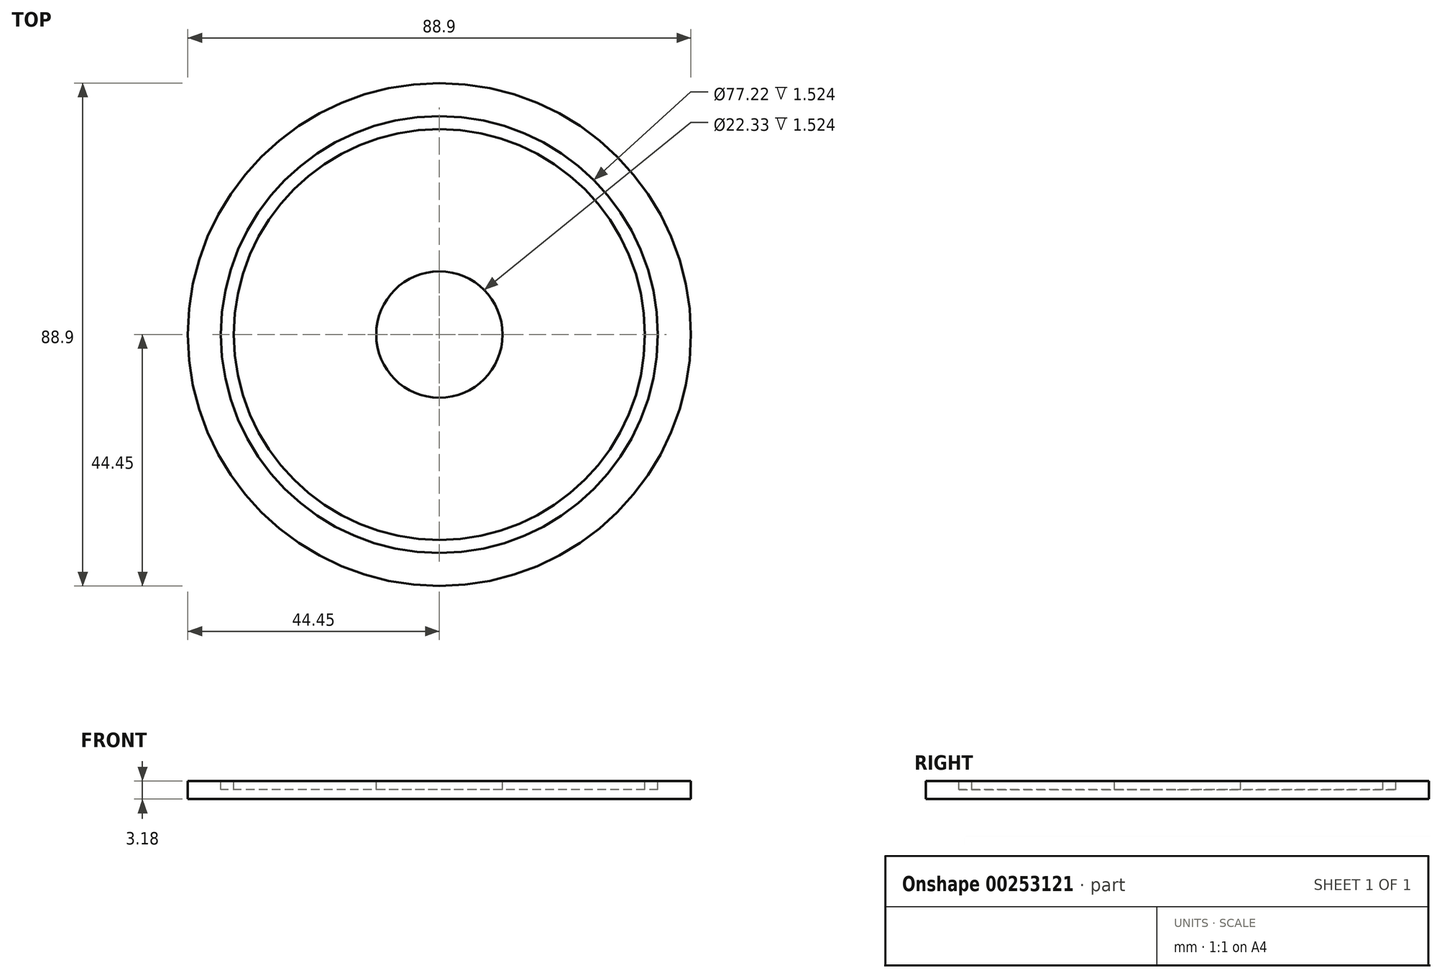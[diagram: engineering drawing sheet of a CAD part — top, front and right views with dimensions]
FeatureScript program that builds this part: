
annotation { "Feature Type Name" : "Feature", "Feature Type Description" : "" }
export const myFeature = defineFeature(function(context is Context, id is Id, definition is map)
    precondition{}
    {
        {
            var Q0;
            Q0=qCreatedBy(makeId("Top.planeOp"),FACE);
            var sketch = newSketch(context, id + "F0", { "sketchPlane" : qUnion([Q0])});
            skCircle(sketch, "E0", {"center": v(0, 0) * mm, "radius": 44.45 * mm});
            skSolve(sketch);
        }
        {
            var Q0;
            Q0=qSketchRegion(id+"F0",true);
            extrude(context, id + "F1", {"entities" : qUnion([Q0]), "depth" : 3.17 * mm});
        }
        {
            var Q0;
            Q0=makeQuery(id+"F1.opExtrude","CAP_FACE",FACE,{"disambiguationData":[OSD([sQuery(id+"F0.wireOp",EDGE,"E0")])],"isStart":false});
            var sketch = newSketch(context, id + "F2", { "sketchPlane" : qUnion([Q0])});
            skCircle(sketch, "E1", {"center": v(0, 0) * mm, "radius": 38.6 * mm});
            skCircle(sketch, "E2", {"center": v(0, 0) * mm, "radius": 36.32 * mm});
            skCircle(sketch, "E3", {"center": v(0, 0) * mm, "radius": 11.16 * mm});
            skSolve(sketch);
        }
        {
            var Q0;
            Q0=qSketchRegion(id+"F2",true);
            var Q1;
            Q1=makeQuery(id+"F2.imprint","IMPRINT",FACE,{"disambiguationData":[TD([[makeQuery(id+"F2.imprint","IMPRINT",EDGE,{"derivedFrom":sQuery(id+"F2.wireOp",EDGE,"E3")}),1.0]])]});
            extrude(context, id + "F3", {"entities" : qUnion([Q0, Q1]), "operationType" : NewBodyOperationType.REMOVE, "oppositeDirection" : true, "depth" : 1.52 * mm});
        }
    });
